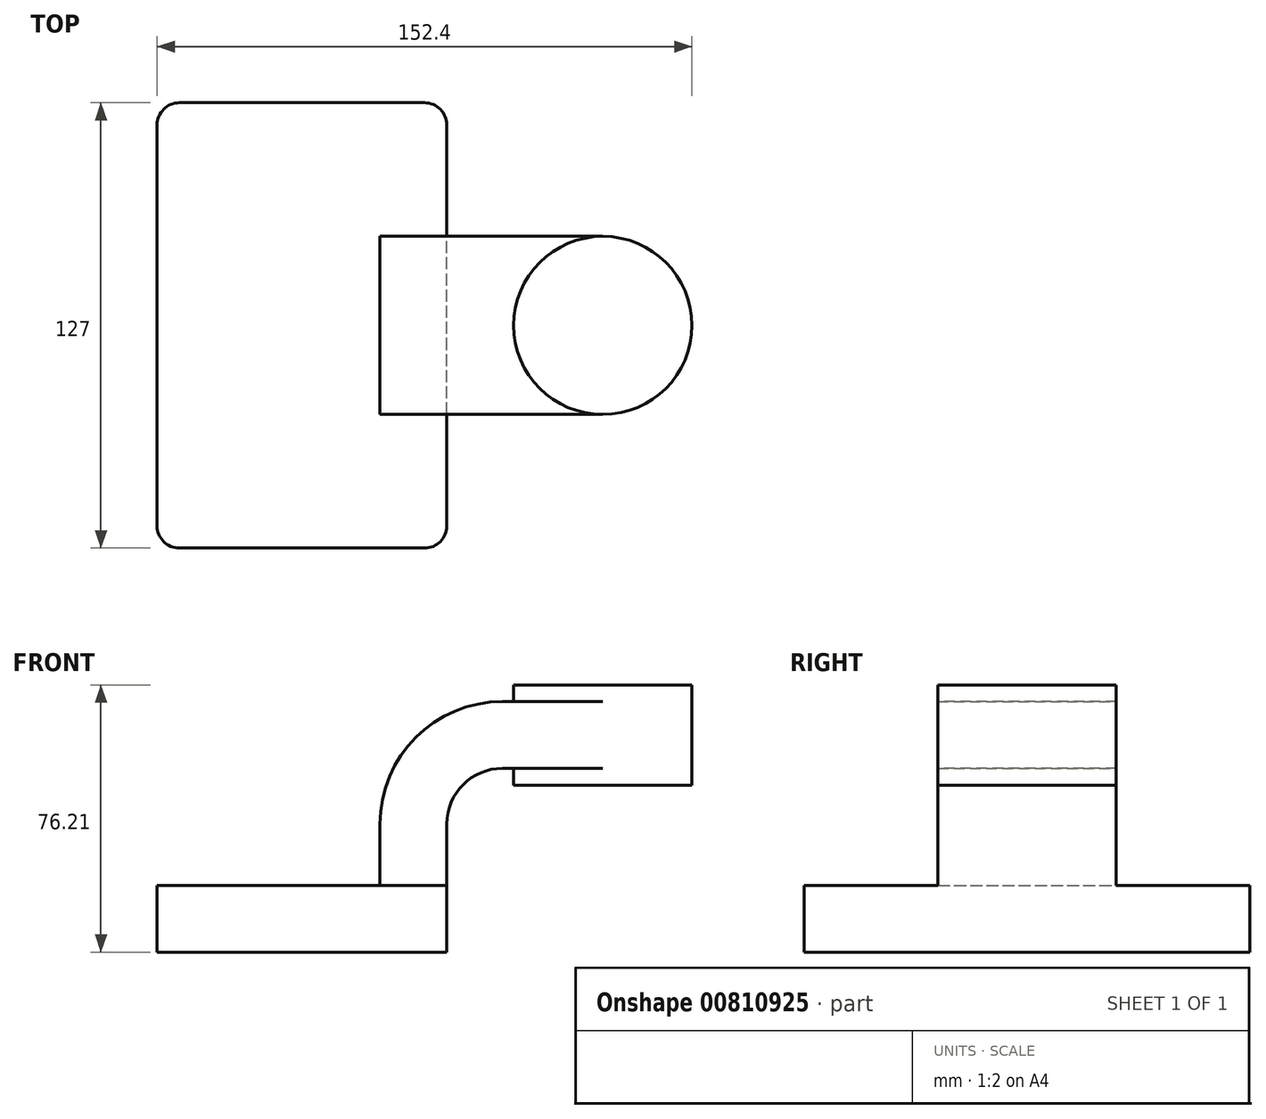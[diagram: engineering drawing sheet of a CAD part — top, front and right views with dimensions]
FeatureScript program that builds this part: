
annotation { "Feature Type Name" : "Feature", "Feature Type Description" : "" }
export const myFeature = defineFeature(function(context is Context, id is Id, definition is map)
    precondition{}
    {
        {
            var Q0;
            Q0=qCreatedBy(makeId("Front.planeOp"),FACE);
            var sketch = newSketch(context, id + "F0", { "sketchPlane" : qUnion([Q0])});
            skLineSegment(sketch, "E0.bottom", {"start": v(-41.28, -9.53) * mm, "end": v(41.28, -9.53) * mm});
            skLineSegment(sketch, "E0.top", {"start": v(-41.28, 9.52) * mm, "end": v(41.28, 9.52) * mm});
            skLineSegment(sketch, "E0.left", {"start": v(-41.27, -9.53) * mm, "end": v(-41.28, 9.52) * mm});
            skLineSegment(sketch, "E0.right", {"start": v(41.28, -9.53) * mm, "end": v(41.28, 9.52) * mm});
            skPoint(sketch, "E0.middle", {"position": v(0, 0) * mm});
            skLineSegment(sketch, "E1.bottom", {"start": v(60.32, 38.1) * mm, "end": v(111.12, 38.1) * mm});
            skLineSegment(sketch, "E1.top", {"start": v(60.32, 66.67) * mm, "end": v(111.12, 66.67) * mm});
            skLineSegment(sketch, "E1.left", {"start": v(60.32, 38.1) * mm, "end": v(60.32, 66.67) * mm});
            skLineSegment(sketch, "E1.right", {"start": v(111.12, 38.1) * mm, "end": v(111.12, 66.67) * mm});
            skPoint(sketch, "E1.middle", {"position": v(85.72, 52.39) * mm});
            skLineSegment(sketch, "E2", {"start": v(41.27, 9.52) * mm, "end": v(41.27, 27) * mm});
            skArc(sketch, "E3", {"start": v(41.28, 27) * mm, "mid": v(45.92, 38.23) * mm, "end": v(57.15, 42.88) * mm});
            skLineSegment(sketch, "E4", {"start": v(57.15, 42.88) * mm, "end": v(85.72, 42.88) * mm});
            skLineSegment(sketch, "E5.0", {"start": v(57.15, 61.93) * mm, "end": v(85.72, 61.93) * mm});
            skArc(sketch, "E5.1", {"start": v(22.23, 27) * mm, "mid": v(32.45, 51.7) * mm, "end": v(57.15, 61.93) * mm});
            skLineSegment(sketch, "E5.2", {"start": v(22.22, 9.52) * mm, "end": v(22.22, 27) * mm});
            skLineSegment(sketch, "E6", {"start": v(85.72, 61.93) * mm, "end": v(85.72, 42.88) * mm});
            skFitSpline(sketch, "E7", {"points": [v(-41.28, 9.53) * mm, v(57.15, 61.93) * mm], "startDerivative": vector(46.61, 105.56) * mm, "endDerivative": vector(137.73, -2.33) * mm});
            skLineSegment(sketch, "E8", {"start": v(85.72, 61.93) * mm, "end": v(85.72, 66.67) * mm});
            skLineSegment(sketch, "E9", {"start": v(85.72, 66.67) * mm, "end": v(85.72, 42.88) * mm});
            skLineSegment(sketch, "E10", {"start": v(85.72, 38.1) * mm, "end": v(85.72, 42.88) * mm});
            skSolve(sketch);
        }
        {
            var Q0;
            Q0=makeQuery(id+"F0.imprint","IMPRINT",FACE,{"disambiguationData":[TD([[makeQuery(id+"F0.imprint","IMPRINT",EDGE,{"derivedFrom":sQuery(id+"F0.wireOp",EDGE,"E0.bottom")}),1.0]])]});
            extrude(context, id + "F1", {"entities" : qUnion([Q0]), "endBound" : BoundingType.SYMMETRIC, "depth" : 127 * mm, "offsetDistance" : 25.4 * mm});
        }
        {
            var Q0;
            {var subQ1=sQuery(id+"F0.wireOp",EDGE,"E2");Q0=makeQuery(id+"F0.imprint","IMPRINT",FACE,{"disambiguationData":[TD([[makeQuery(id+"F0.imprint","IMPRINT",EDGE,{"derivedFrom":subQ1}),1.0]])]});}
            var Q1;
            {var subQ0=sQuery(id+"F0.wireOp",EDGE,"E4");var subQ1=sQuery(id+"F0.wireOp",EDGE,"E1.left");var subQ2=makeQuery(id+"F0.imprint","INTERSECT",VERTEX,{"derivedFrom":[subQ1,subQ0]});Q1=makeQuery(id+"F0.imprint","IMPRINT",FACE,{"disambiguationData":[TD([[makeQuery(id+"F0.imprint","IMPRINT",EDGE,{"disambiguationData":[TD([[subQ2,-1.0]])],"derivedFrom":subQ1}),-1.0]])]});}
            extrude(context, id + "F2", {"entities" : qUnion([Q0, Q1]), "operationType" : NewBodyOperationType.ADD, "endBound" : BoundingType.SYMMETRIC, "depth" : 50.8 * mm, "offsetDistance" : 25.4 * mm});
        }
        {
            var Q0;
            Q0=makeQuery(id+"F0.imprint","IMPRINT",FACE,{"disambiguationData":[TD([[makeQuery(id+"F0.imprint","IMPRINT",EDGE,{"derivedFrom":sQuery(id+"F0.wireOp",EDGE,"E5.1")}),1.0]])]});
            extrude(context, id + "F3", {"entities" : qUnion([Q0]), "operationType" : NewBodyOperationType.ADD, "endBound" : BoundingType.SYMMETRIC, "depth" : 15.88 * mm, "offsetDistance" : 25.4 * mm});
        }
        {
            var Q0;
            {var subQ4=sQuery(id+"F0.wireOp",EDGE,"E1.right");Q0=makeQuery(id+"F0.imprint","IMPRINT",FACE,{"disambiguationData":[TD([[makeQuery(id+"F0.imprint","IMPRINT",EDGE,{"derivedFrom":subQ4}),1.0]])]});}
            var Q1;
            Q1=sQuery(id+"F0.wireOp",EDGE,"E9");
            revolve(context, id + "F4", {"operationType" : NewBodyOperationType.ADD, "surfaceOperationType" : NewSurfaceOperationType.NEW, "entities" : qUnion([Q0]), "axis" : qUnion([Q1]), "revolveType" : RevolveType.FULL});
        }
        {
            var Q0;
            Q0=makeQuery(id+"F1.opExtrude","CAP_EDGE",EDGE,{"disambiguationData":[OSD([sQuery(id+"F0.wireOp",EDGE,"E0.right")])],"isStart":false});
            var Q1;
            Q1=makeQuery(id+"F1.opExtrude","CAP_EDGE",EDGE,{"disambiguationData":[OSD([sQuery(id+"F0.wireOp",EDGE,"E0.left")])],"isStart":false});
            var Q2;
            Q2=makeQuery(id+"F1.opExtrude","CAP_EDGE",EDGE,{"disambiguationData":[OSD([sQuery(id+"F0.wireOp",EDGE,"E0.right")])],"isStart":true});
            var Q3;
            Q3=makeQuery(id+"F1.opExtrude","CAP_EDGE",EDGE,{"disambiguationData":[OSD([sQuery(id+"F0.wireOp",EDGE,"E0.left")])],"isStart":true});
            fillet(context, id + "F5", {"entities" : qUnion([Q0, Q1, Q2, Q3]), "radius" : 6.35 * mm, "tangentPropagation" : true, "allowEdgeOverflow" : false});
        }
    });
